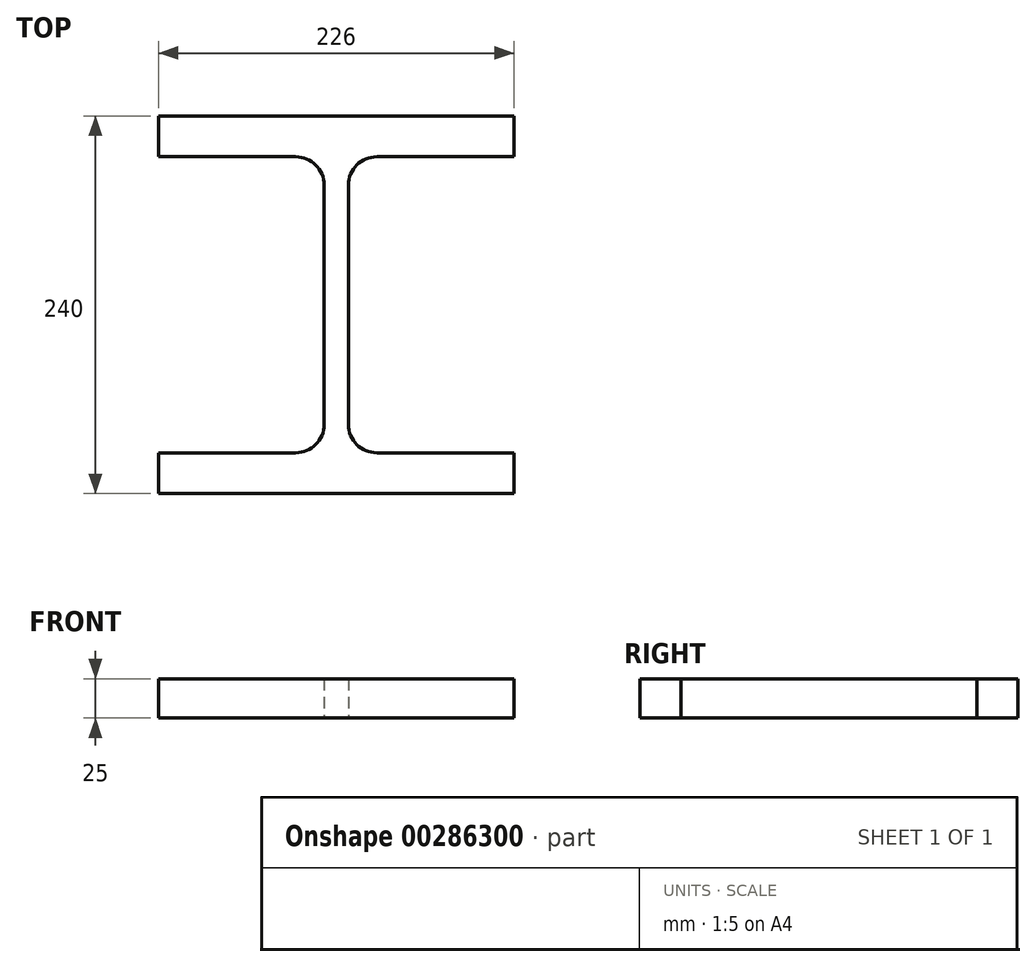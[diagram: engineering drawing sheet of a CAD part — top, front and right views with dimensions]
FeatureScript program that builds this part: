
annotation { "Feature Type Name" : "Feature", "Feature Type Description" : "" }
export const myFeature = defineFeature(function(context is Context, id is Id, definition is map)
    precondition{}
    {
        {
            var Q0;
            Q0=qCreatedBy(makeId("Top.planeOp"),FACE);
            var sketch = newSketch(context, id + "F0", { "sketchPlane" : qUnion([Q0])});
            skLineSegment(sketch, "E0", {"start": v(0, 0) * mm, "end": v(226, 0) * mm});
            skLineSegment(sketch, "E1", {"start": v(226, 0) * mm, "end": v(226, -26) * mm});
            skLineSegment(sketch, "E2", {"start": v(226, -26) * mm, "end": v(138.75, -26) * mm});
            skLineSegment(sketch, "E3", {"start": v(0, 0) * mm, "end": v(0, -26) * mm});
            skLineSegment(sketch, "E4", {"start": v(0, -26) * mm, "end": v(87.25, -26) * mm});
            skLineSegment(sketch, "E5", {"start": v(105.25, -44) * mm, "end": v(105.25, -196) * mm});
            skLineSegment(sketch, "E6", {"start": v(87.25, -214) * mm, "end": v(0, -214) * mm});
            skLineSegment(sketch, "E7", {"start": v(0, -214) * mm, "end": v(0, -240) * mm});
            skLineSegment(sketch, "E8", {"start": v(0, -240) * mm, "end": v(226, -240) * mm});
            skLineSegment(sketch, "E9", {"start": v(226, -240) * mm, "end": v(226, -214) * mm});
            skLineSegment(sketch, "E10", {"start": v(226, -214) * mm, "end": v(138.75, -214) * mm});
            skLineSegment(sketch, "E11", {"start": v(120.75, -196) * mm, "end": v(120.75, -44) * mm});
            skPoint(sketch, "E12.visualSharp", {"position": v(105.25, -26) * mm});
            skArc(sketch, "E12.filletArc", {"start": v(105.25, -44) * mm, "mid": v(99.98, -31.27) * mm, "end": v(87.25, -26) * mm});
            skPoint(sketch, "E13.visualSharp", {"position": v(105.25, -214) * mm});
            skArc(sketch, "E13.filletArc", {"start": v(87.25, -214) * mm, "mid": v(99.98, -208.73) * mm, "end": v(105.25, -196) * mm});
            skPoint(sketch, "E14.visualSharp", {"position": v(120.75, -214) * mm});
            skArc(sketch, "E14.filletArc", {"start": v(120.75, -196) * mm, "mid": v(126.02, -208.73) * mm, "end": v(138.75, -214) * mm});
            skPoint(sketch, "E15.visualSharp", {"position": v(120.75, -26) * mm});
            skArc(sketch, "E15.filletArc", {"start": v(138.75, -26) * mm, "mid": v(126.02, -31.27) * mm, "end": v(120.75, -44) * mm});
            skSolve(sketch);
        }
        {
            var Q0;
            Q0=makeQuery(id+"F0.imprint","IMPRINT",FACE,{"disambiguationData":[TD([[makeQuery(id+"F0.imprint","IMPRINT",EDGE,{"derivedFrom":sQuery(id+"F0.wireOp",EDGE,"E0")}),-1.0]])]});
            extrude(context, id + "F1", {"entities" : qUnion([Q0]), "depth" : 25 * mm});
        }
    });
